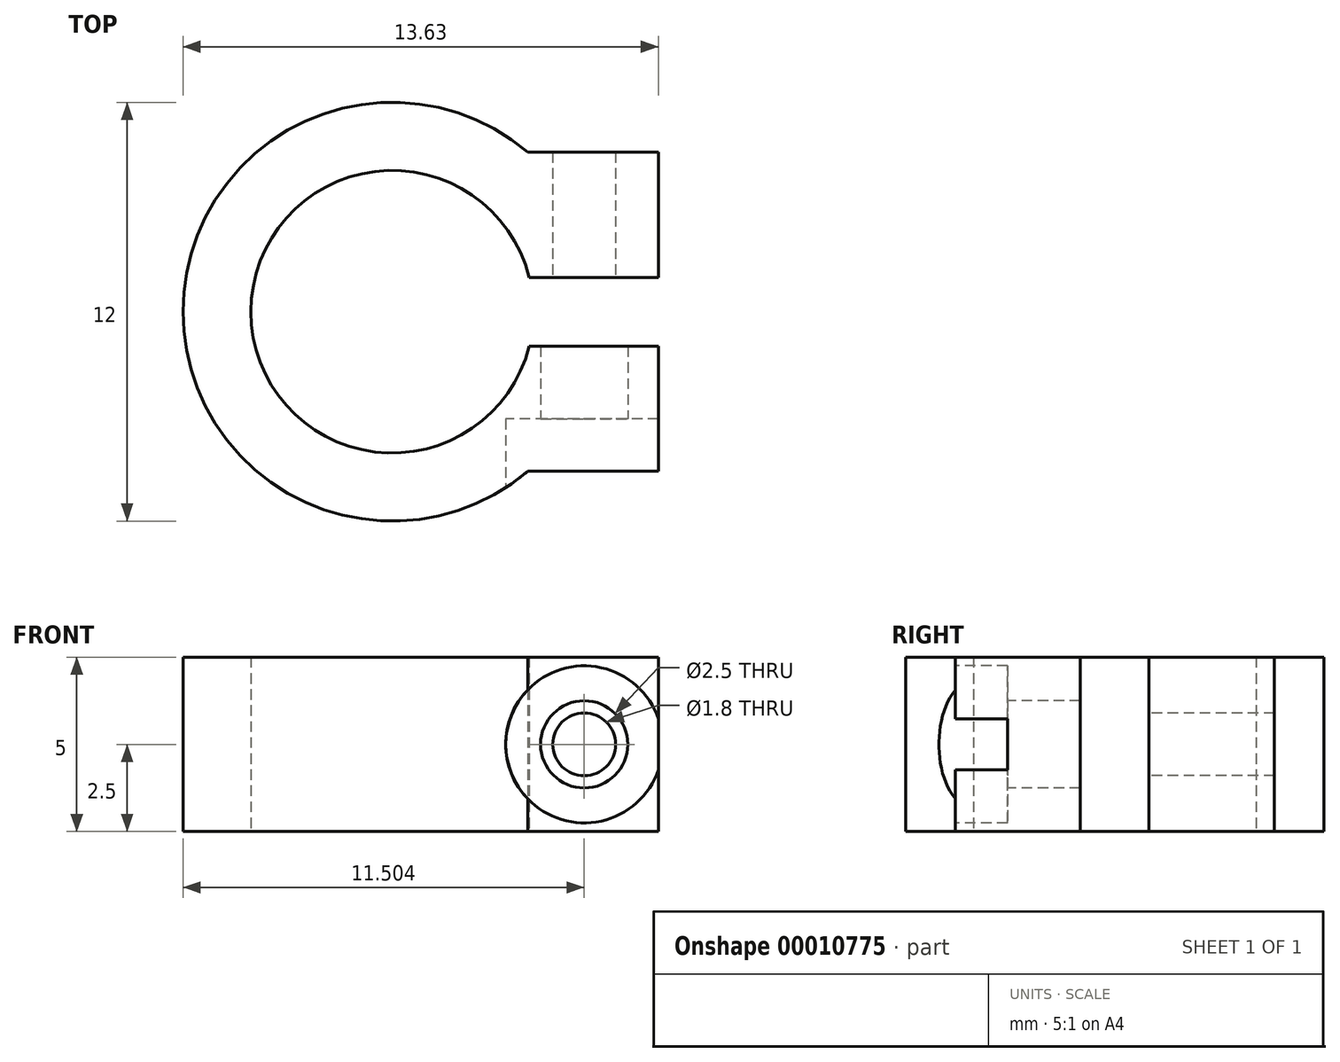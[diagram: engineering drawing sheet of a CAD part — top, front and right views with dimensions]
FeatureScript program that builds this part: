
annotation { "Feature Type Name" : "Feature", "Feature Type Description" : "" }
export const myFeature = defineFeature(function(context is Context, id is Id, definition is map)
    precondition{}
    {
        {
            var Q0;
            Q0=qCreatedBy(makeId("Top.planeOp"),FACE);
            var sketch = newSketch(context, id + "F0", { "sketchPlane" : qUnion([Q0])});
            skArc(sketch, "E0", {"start": v(3.88, 4.58) * mm, "mid": v(-6, 0) * mm, "end": v(3.88, -4.58) * mm});
            skArc(sketch, "E1", {"start": v(3.93, 0.98) * mm, "mid": v(-4.05, 0) * mm, "end": v(3.93, -1) * mm});
            skLineSegment(sketch, "E2.bottom", {"start": v(3.88, 4.58) * mm, "end": v(7.63, 4.58) * mm});
            skLineSegment(sketch, "E2.top", {"start": v(3.88, -4.58) * mm, "end": v(7.63, -4.58) * mm});
            skLineSegment(sketch, "E2.right", {"start": v(7.63, 4.58) * mm, "end": v(7.63, 0.98) * mm});
            skLineSegment(sketch, "E3.bottom", {"start": v(3.93, 0.98) * mm, "end": v(7.63, 0.98) * mm});
            skLineSegment(sketch, "E3.top", {"start": v(3.93, -1) * mm, "end": v(7.63, -1) * mm});
            skLineSegment(sketch, "E4.trimOffspring", {"start": v(7.63, -1) * mm, "end": v(7.63, -4.58) * mm});
            skSolve(sketch);
        }
        {
            var Q0;
            Q0 = qSketchRegion(id + "F0", true);
            extrude(context, id + "F1", {"entities" : qUnion([Q0]), "depth" : 5 * mm});
        }
        {
            var Q0;
            Q0=makeQuery(id+"F1.opExtrude","SWEPT_FACE",FACE,{"disambiguationData":[OSD([sQuery(id+"F0.wireOp",EDGE,"E2.top")])]});
            var sketch = newSketch(context, id + "F2", { "sketchPlane" : qUnion([Q0])});
            skCircle(sketch, "E5", {"center": v(5.5, 2.5) * mm, "radius": 0.9 * mm});
            skPoint(sketch, "E5.centerSnap0", {"position": v(3.88, 2.5) * mm});
            skSolve(sketch);
        }
        {
            var Q0;
            Q0 = qSketchRegion(id + "F2", true);
            extrude(context, id + "F3", {"entities" : qUnion([Q0]), "operationType" : NewBodyOperationType.REMOVE, "endBound" : BoundingType.SYMMETRIC, "oppositeDirection" : true, "depth" : 25 * mm});
        }
        {
            var Q0;
            Q0=makeQuery(id+"F1.opExtrude","SWEPT_FACE",FACE,{"disambiguationData":[OSD([sQuery(id+"F0.wireOp",EDGE,"E2.top")])]});
            var sketch = newSketch(context, id + "F4", { "sketchPlane" : qUnion([Q0])});
            skCircle(sketch, "E6", {"center": v(5.5, 2.5) * mm, "radius": 1.25 * mm});
            skSolve(sketch);
        }
        {
            var Q0;
            Q0 = qSketchRegion(id + "F4", true);
            extrude(context, id + "F5", {"entities" : qUnion([Q0]), "operationType" : NewBodyOperationType.REMOVE, "endBound" : BoundingType.SYMMETRIC, "oppositeDirection" : true, "depth" : 8 * mm});
        }
        {
            var Q0;
            Q0=makeQuery(id+"F1.opExtrude","SWEPT_FACE",FACE,{"disambiguationData":[OSD([sQuery(id+"F0.wireOp",EDGE,"E2.top")])]});
            var sketch = newSketch(context, id + "F6", { "sketchPlane" : qUnion([Q0])});
            skCircle(sketch, "E7", {"center": v(5.5, 2.5) * mm, "radius": 2.25 * mm});
            skSolve(sketch);
        }
        {
            var Q0;
            Q0 = qSketchRegion(id + "F6", true);
            extrude(context, id + "F7", {"entities" : qUnion([Q0]), "operationType" : NewBodyOperationType.REMOVE, "endBound" : BoundingType.SYMMETRIC, "oppositeDirection" : true, "depth" : 3 * mm});
        }
    });
